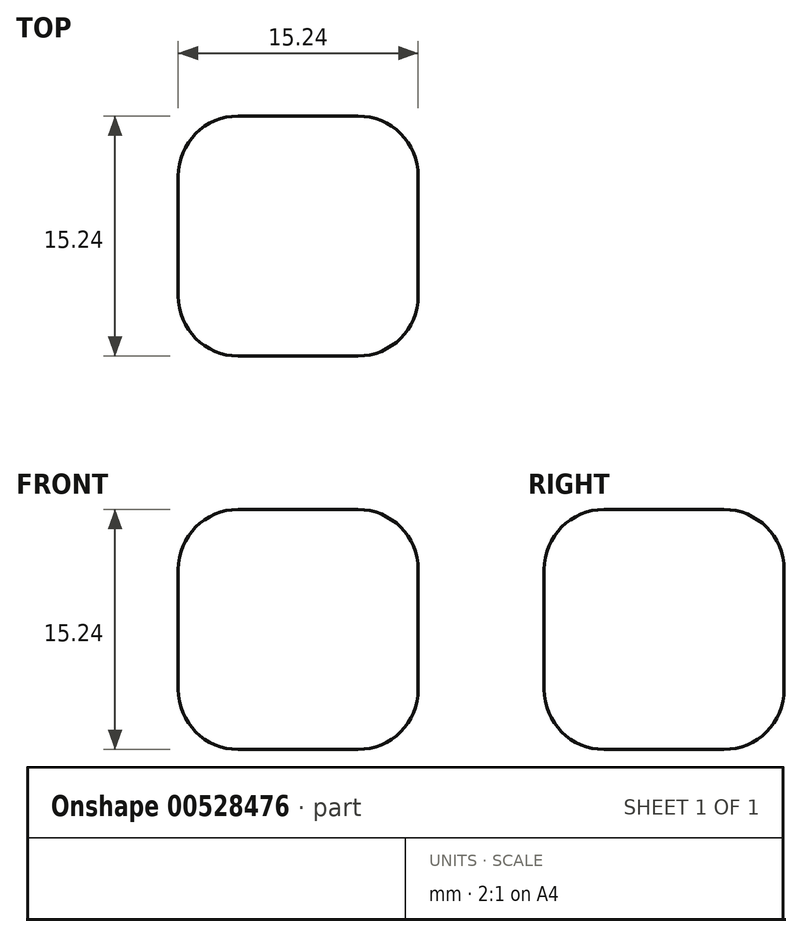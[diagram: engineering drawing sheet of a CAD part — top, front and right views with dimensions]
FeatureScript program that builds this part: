
annotation { "Feature Type Name" : "Feature", "Feature Type Description" : "" }
export const myFeature = defineFeature(function(context is Context, id is Id, definition is map)
    precondition{}
    {
        {
            var Q0;
            Q0=qCreatedBy(makeId("Top.planeOp"),FACE);
            var sketch = newSketch(context, id + "F0", { "sketchPlane" : qUnion([Q0])});
            skLineSegment(sketch, "E0.bottom", {"start": v(3.81, -7.62) * mm, "end": v(-3.81, -7.62) * mm});
            skLineSegment(sketch, "E0.top", {"start": v(3.8, 7.62) * mm, "end": v(-3.81, 7.62) * mm});
            skLineSegment(sketch, "E0.left", {"start": v(7.62, -3.81) * mm, "end": v(7.62, 3.81) * mm});
            skLineSegment(sketch, "E0.right", {"start": v(-7.62, -3.81) * mm, "end": v(-7.62, 3.81) * mm});
            skPoint(sketch, "E0.middle", {"position": v(0, 0) * mm});
            skPoint(sketch, "E1.visualSharp", {"position": v(-7.62, 7.62) * mm});
            skArc(sketch, "E1.filletArc", {"start": v(-3.81, 7.62) * mm, "mid": v(-6.5, 6.5) * mm, "end": v(-7.62, 3.81) * mm});
            skPoint(sketch, "E2.visualSharp", {"position": v(7.62, 7.62) * mm});
            skArc(sketch, "E2.filletArc", {"start": v(7.62, 3.81) * mm, "mid": v(6.5, 6.5) * mm, "end": v(3.8, 7.62) * mm});
            skPoint(sketch, "E3.visualSharp", {"position": v(7.62, -7.62) * mm});
            skArc(sketch, "E3.filletArc", {"start": v(3.81, -7.62) * mm, "mid": v(6.5, -6.5) * mm, "end": v(7.62, -3.81) * mm});
            skPoint(sketch, "E4.visualSharp", {"position": v(-7.62, -7.62) * mm});
            skArc(sketch, "E4.filletArc", {"start": v(-7.62, -3.81) * mm, "mid": v(-6.5, -6.5) * mm, "end": v(-3.81, -7.62) * mm});
            skSolve(sketch);
        }
        {
            var Q0;
            Q0=makeQuery(id+"F0.imprint","IMPRINT",FACE,{"disambiguationData":[TD([[makeQuery(id+"F0.imprint","IMPRINT",EDGE,{"derivedFrom":sQuery(id+"F0.wireOp",EDGE,"E0.bottom")}),-1.0]])]});
            extrude(context, id + "F1", {"entities" : qUnion([Q0]), "depth" : 15.24 * mm, "offsetDistance" : 25.4 * mm});
        }
        {
            var Q0;
            Q0=makeQuery(id+"F1.opExtrude","CAP_FACE",FACE,{"disambiguationData":[OSD([sQuery(id+"F0.wireOp",EDGE,"E0.bottom"),sQuery(id+"F0.wireOp",EDGE,"E0.top"),sQuery(id+"F0.wireOp",EDGE,"E0.left"),sQuery(id+"F0.wireOp",EDGE,"E0.right"),sQuery(id+"F0.wireOp",EDGE,"E1.filletArc"),sQuery(id+"F0.wireOp",EDGE,"E2.filletArc"),sQuery(id+"F0.wireOp",EDGE,"E3.filletArc"),sQuery(id+"F0.wireOp",EDGE,"E4.filletArc")])],"isStart":false});
            var Q1;
            Q1=makeQuery(id+"F1.opExtrude","CAP_FACE",FACE,{"disambiguationData":[OSD([sQuery(id+"F0.wireOp",EDGE,"E0.bottom"),sQuery(id+"F0.wireOp",EDGE,"E0.top"),sQuery(id+"F0.wireOp",EDGE,"E0.left"),sQuery(id+"F0.wireOp",EDGE,"E0.right"),sQuery(id+"F0.wireOp",EDGE,"E1.filletArc"),sQuery(id+"F0.wireOp",EDGE,"E2.filletArc"),sQuery(id+"F0.wireOp",EDGE,"E3.filletArc"),sQuery(id+"F0.wireOp",EDGE,"E4.filletArc")])],"isStart":true});
            fillet(context, id + "F2", {"entities" : qUnion([Q0, Q1]), "radius" : 3.8 * mm, "tangentPropagation" : true, "allowEdgeOverflow" : false});
        }
    });
